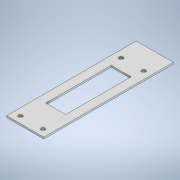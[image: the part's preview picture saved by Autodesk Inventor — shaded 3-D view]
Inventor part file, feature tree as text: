
AUTODESK INVENTOR PART (.ipt)
format: ipt  version: 2022 (Build 260153000, 153)  size: 180,736 bytes
history: native  units: in
note: dims shown in document units (in); Inventor stores cm internally (conversion verified against a paired STEP export)
features: extrude x1, sketch x1
ambient origin geometry x8: Origin, YZ Plane, XZ Plane, XY Plane, X Axis, Y Axis, Z Axis, Center Point
bodies: Body1 (feature_tree)
feature tree (2):
  extrude  "Extrusion2"  Depth=0.0625in
  sketch  "Sketch1"  dims[d0=0.003in d1=0.0625in d2=0.15in d3=4.2322in d4=6.13in d5=0.0699in d6=0.0699in d7=0.0699in d10=0.0625in d11=0.0in]
